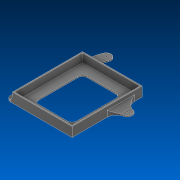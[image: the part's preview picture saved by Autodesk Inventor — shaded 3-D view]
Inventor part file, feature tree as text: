
AUTODESK INVENTOR PART (.ipt)
format: ipt  version: 2022.2 (Build 262287000, 287)  size: 190,976 bytes
history: native  units: in
note: dims shown in document units (in); Inventor stores cm internally (conversion verified against a paired STEP export)
features: extrude x3, sketch x3, fillet x2, hole x1, projected_geometry x1
ambient origin geometry x8: Origin, YZ Plane, XZ Plane, XY Plane, X Axis, Y Axis, Z Axis, Center Point
bodies: Solid1 (feature_tree)
feature tree (10):
  extrude  "Extrusion1"  Depth=1.0in
  extrude  "Extrusion2"  Depth=7.1in
  sketch  "Sketch4"  dims[d4=0.125in d5=0.0in d6=0.125in d7=1.0in d8=0.0in d9=1.0in d10=0.175in d11=0.6859in d12=1.65in d14=5.1109in d15=0.5in d16=0.125in d17=0.0in d18=0.175in d19=0.75in d20=0.35in d21=0.0in d22=0.5635in d23=1.0in d24=0.8108in d26=0.825in d27=0.5in d28=0.5in]
  extrude  "Extrusion3"  Depth=0.125in
  fillet  "Fillet1"  Radius=1.0in
  hole  "Hole1"  [1 undecoded]
  fillet  "Fillet2"  Radius=0.175in
  sketch  "Sketch1"  dims[d0=1.0in d1=1.0in]
  sketch  "Sketch3"  dims[d2=6.0in d3=7.1in]
  projected_geometry  "Projected Loop1"
note: 1 required parameter value undecoded (feature->parameter linkage not recoverable at this tier; creation-order binding heuristic only, values carry confidence <= 0.55)
